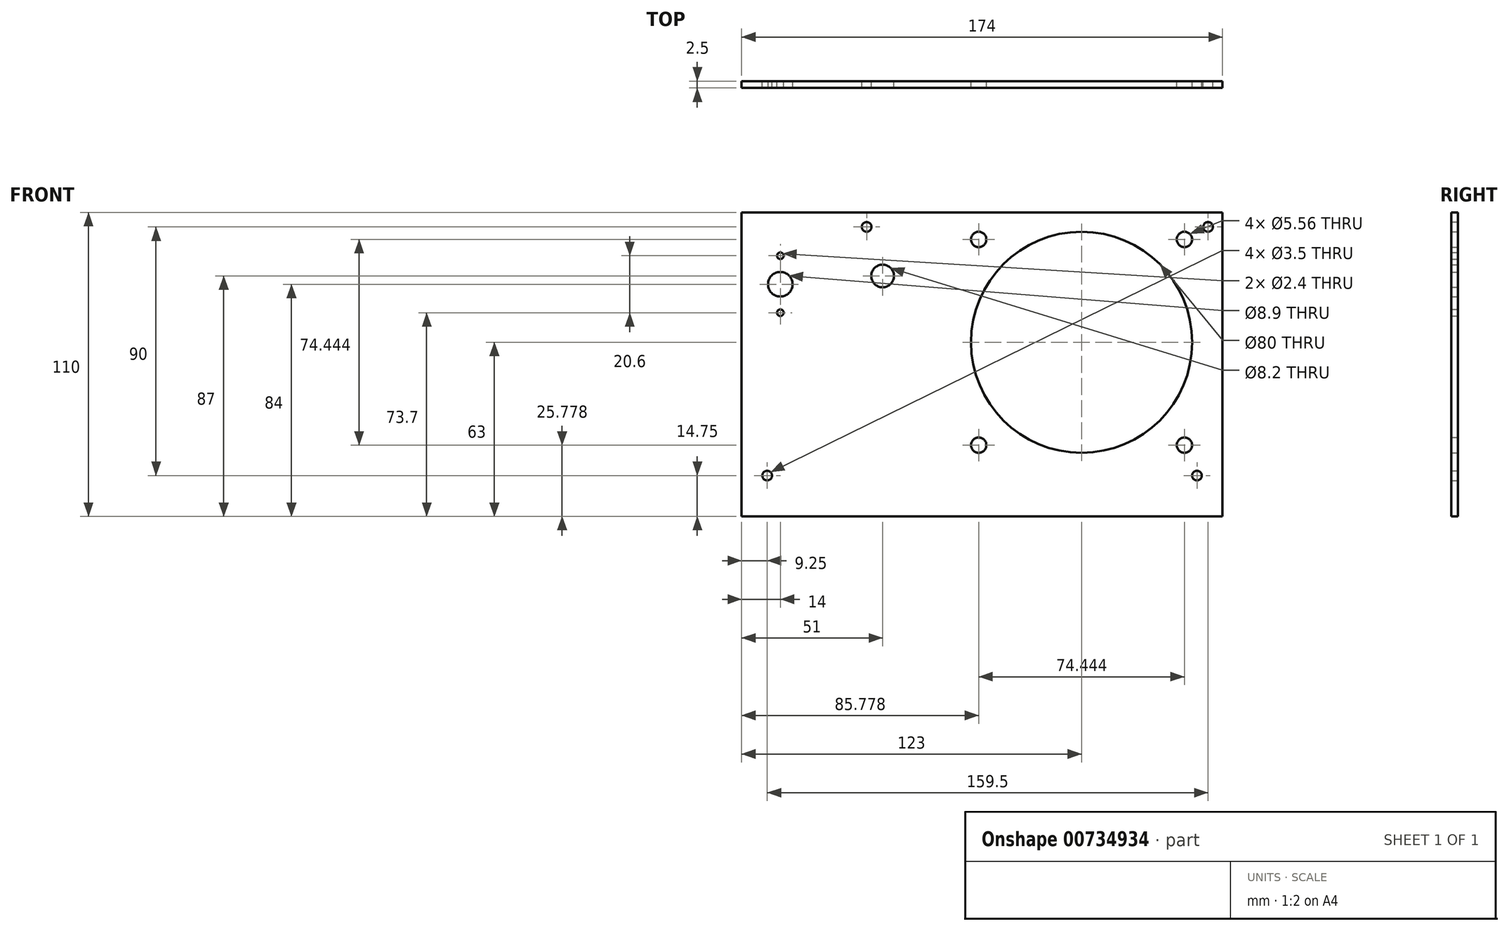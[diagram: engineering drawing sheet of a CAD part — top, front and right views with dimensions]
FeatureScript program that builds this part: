
annotation { "Feature Type Name" : "Feature", "Feature Type Description" : "" }
export const myFeature = defineFeature(function(context is Context, id is Id, definition is map)
    precondition{}
    {
        {
            var Q0;
            Q0=qCreatedBy(makeId("Front.planeOp"),FACE);
            var sketch = newSketch(context, id + "F0", { "sketchPlane" : qUnion([Q0])});
            skLineSegment(sketch, "E0.bottom", {"start": v(-87, -55) * mm, "end": v(87, -55) * mm});
            skLineSegment(sketch, "E0.top", {"start": v(-87, 55) * mm, "end": v(87, 55) * mm});
            skLineSegment(sketch, "E0.left", {"start": v(-87, -55) * mm, "end": v(-87, 55) * mm});
            skLineSegment(sketch, "E0.right", {"start": v(87, -55) * mm, "end": v(87, 55) * mm});
            skPoint(sketch, "E0.middle", {"position": v(0, 0) * mm});
            skLineSegment(sketch, "E1.bottom", {"start": v(-80, 44) * mm, "end": v(-66, 44) * mm, "construction": true});
            skLineSegment(sketch, "E1.top", {"start": v(-80, 14) * mm, "end": v(-66, 14) * mm, "construction": true});
            skLineSegment(sketch, "E1.left", {"start": v(-80, 44) * mm, "end": v(-80, 14) * mm, "construction": true});
            skLineSegment(sketch, "E1.right", {"start": v(-66, 44) * mm, "end": v(-66, 14) * mm, "construction": true});
            skLineSegment(sketch, "E2.bottom", {"start": v(-51, 43) * mm, "end": v(-21, 43) * mm, "construction": true});
            skLineSegment(sketch, "E2.top", {"start": v(-51, 21) * mm, "end": v(-21, 21) * mm, "construction": true});
            skLineSegment(sketch, "E2.left", {"start": v(-51, 43) * mm, "end": v(-51, 21) * mm, "construction": true});
            skLineSegment(sketch, "E2.right", {"start": v(-21, 43) * mm, "end": v(-21, 21) * mm, "construction": true});
            skCircle(sketch, "E3", {"center": v(-77.75, -40.25) * mm, "radius": 1.75 * mm});
            skCircle(sketch, "E4", {"center": v(81.75, 49.75) * mm, "radius": 1.75 * mm});
            skCircle(sketch, "E5", {"center": v(-41.75, 49.75) * mm, "radius": 1.75 * mm});
            skCircle(sketch, "E6", {"center": v(77.75, -40.25) * mm, "radius": 1.75 * mm});
            skLineSegment(sketch, "E7.bottom", {"start": v(76, -32) * mm, "end": v(-4, -32) * mm, "construction": true});
            skLineSegment(sketch, "E7.top", {"start": v(76, 48) * mm, "end": v(-4, 48) * mm, "construction": true});
            skLineSegment(sketch, "E7.left", {"start": v(76, -32) * mm, "end": v(76, 48) * mm, "construction": true});
            skLineSegment(sketch, "E7.right", {"start": v(-4, -32) * mm, "end": v(-4, 48) * mm, "construction": true});
            skCircle(sketch, "E8", {"center": v(36, 8) * mm, "radius": 40 * mm});
            skPoint(sketch, "E8.first.point", {"position": v(36, 48) * mm});
            skPoint(sketch, "E8.second.point", {"position": v(76, 8) * mm});
            skPoint(sketch, "E8.third.point", {"position": v(36, -32) * mm});
            skLineSegment(sketch, "E9.bottom", {"start": v(-4, 48) * mm, "end": v(1.56, 48) * mm, "construction": true});
            skLineSegment(sketch, "E9.top", {"start": v(-4, 42.44) * mm, "end": v(1.56, 42.44) * mm, "construction": true});
            skLineSegment(sketch, "E9.left", {"start": v(-4, 48) * mm, "end": v(-4, 42.44) * mm, "construction": true});
            skLineSegment(sketch, "E9.right", {"start": v(1.56, 48) * mm, "end": v(1.56, 42.44) * mm, "construction": true});
            skCircle(sketch, "E10", {"center": v(-1.22, 45.22) * mm, "radius": 2.78 * mm});
            skPoint(sketch, "E10.first.point", {"position": v(-1.22, 48) * mm});
            skPoint(sketch, "E10.second.point", {"position": v(1.56, 45.22) * mm});
            skPoint(sketch, "E10.third.point", {"position": v(-1.22, 42.44) * mm});
            skLineSegment(sketch, "E11.bottom", {"start": v(76, 48) * mm, "end": v(70.44, 48) * mm, "construction": true});
            skLineSegment(sketch, "E11.top", {"start": v(76, 42.44) * mm, "end": v(70.44, 42.44) * mm, "construction": true});
            skLineSegment(sketch, "E11.left", {"start": v(76, 48) * mm, "end": v(76, 42.44) * mm, "construction": true});
            skLineSegment(sketch, "E11.right", {"start": v(70.44, 48) * mm, "end": v(70.44, 42.44) * mm, "construction": true});
            skLineSegment(sketch, "E12.bottom", {"start": v(76, -32) * mm, "end": v(70.44, -32) * mm, "construction": true});
            skLineSegment(sketch, "E12.top", {"start": v(76, -26.44) * mm, "end": v(70.44, -26.44) * mm, "construction": true});
            skLineSegment(sketch, "E12.left", {"start": v(76, -32) * mm, "end": v(76, -26.44) * mm, "construction": true});
            skLineSegment(sketch, "E12.right", {"start": v(70.44, -32) * mm, "end": v(70.44, -26.44) * mm, "construction": true});
            skLineSegment(sketch, "E13.bottom", {"start": v(-4, -32) * mm, "end": v(1.56, -32) * mm, "construction": true});
            skLineSegment(sketch, "E13.top", {"start": v(-4, -26.44) * mm, "end": v(1.56, -26.44) * mm, "construction": true});
            skLineSegment(sketch, "E13.left", {"start": v(-4, -32) * mm, "end": v(-4, -26.44) * mm, "construction": true});
            skLineSegment(sketch, "E13.right", {"start": v(1.56, -32) * mm, "end": v(1.56, -26.44) * mm, "construction": true});
            skCircle(sketch, "E14", {"center": v(73.22, 45.22) * mm, "radius": 2.78 * mm});
            skPoint(sketch, "E14.first.point", {"position": v(73.22, 48) * mm});
            skPoint(sketch, "E14.second.point", {"position": v(70.44, 45.22) * mm});
            skPoint(sketch, "E14.third.point", {"position": v(73.22, 42.44) * mm});
            skCircle(sketch, "E15", {"center": v(73.22, -29.22) * mm, "radius": 2.78 * mm});
            skPoint(sketch, "E15.first.point", {"position": v(73.22, -26.44) * mm});
            skPoint(sketch, "E15.second.point", {"position": v(70.44, -29.22) * mm});
            skPoint(sketch, "E15.third.point", {"position": v(73.22, -32) * mm});
            skCircle(sketch, "E16", {"center": v(-1.22, -29.22) * mm, "radius": 2.78 * mm});
            skPoint(sketch, "E16.first.point", {"position": v(-1.22, -26.44) * mm});
            skPoint(sketch, "E16.second.point", {"position": v(-4, -29.22) * mm});
            skPoint(sketch, "E16.third.point", {"position": v(-1.22, -32) * mm});
            skPoint(sketch, "E17", {"position": v(-80, 29) * mm});
            skPoint(sketch, "E18", {"position": v(-73, 14) * mm});
            skPoint(sketch, "E19", {"position": v(-73, 29) * mm});
            skCircle(sketch, "E20", {"center": v(-73, 29) * mm, "radius": 4.45 * mm});
            skLineSegment(sketch, "E21", {"start": v(-73, 18.7) * mm, "end": v(-73, 39.3) * mm, "construction": true});
            skCircle(sketch, "E22", {"center": v(-73, 39.3) * mm, "radius": 1.2 * mm});
            skCircle(sketch, "E23", {"center": v(-73, 18.7) * mm, "radius": 1.2 * mm});
            skPoint(sketch, "E24", {"position": v(-51, 32) * mm});
            skPoint(sketch, "E25", {"position": v(-36, 21) * mm});
            skPoint(sketch, "E26", {"position": v(-36, 32) * mm});
            skCircle(sketch, "E27", {"center": v(-36, 32) * mm, "radius": 4.1 * mm});
            skSolve(sketch);
        }
        {
            var Q0;
            {var subQ0=sQuery(id+"F0.wireOp",EDGE,"cfSl68OW-Y9iN-8OMg-qRQz-4nlVoakqv04e");var subQ1=sQuery(id+"F0.wireOp",EDGE,"vP8uru67-1rKL-aZWj-Ed0x-q8X2hZfk60Cs.left");var subQ2=makeQuery(id+"F0.imprint","INTERSECT",VERTEX,{"derivedFrom":[subQ1,subQ0]});Q0=makeQuery(id+"F0.imprint","IMPRINT",FACE,{"disambiguationData":[TD([[makeQuery(id+"F0.imprint","IMPRINT",EDGE,{"disambiguationData":[TD([[subQ2,1.0]])],"derivedFrom":subQ1}),-1.0]])]});}
            var Q1;
            {var subQ0=sQuery(id+"F0.wireOp",EDGE,"cfSl68OW-Y9iN-8OMg-qRQz-4nlVoakqv04e");var subQ1=sQuery(id+"F0.wireOp",EDGE,"vP8uru67-1rKL-aZWj-Ed0x-q8X2hZfk60Cs.bottom");var subQ2=makeQuery(id+"F0.imprint","INTERSECT",VERTEX,{"derivedFrom":[subQ1,subQ0]});Q1=makeQuery(id+"F0.imprint","IMPRINT",FACE,{"disambiguationData":[TD([[makeQuery(id+"F0.imprint","IMPRINT",EDGE,{"disambiguationData":[TD([[subQ2,1.0]])],"derivedFrom":subQ1}),1.0]])]});}
            var Q2;
            {var subQ0=sQuery(id+"F0.wireOp",EDGE,"PTcjDCUc-MgrD-nLkz-FqYk-Pj8Vo6t2aX3y");var subQ1=sQuery(id+"F0.wireOp",EDGE,"vP8uru67-1rKL-aZWj-Ed0x-q8X2hZfk60Cs.left");var subQ2=makeQuery(id+"F0.imprint","INTERSECT",VERTEX,{"derivedFrom":[subQ1,subQ0]});Q2=makeQuery(id+"F0.imprint","IMPRINT",FACE,{"disambiguationData":[TD([[makeQuery(id+"F0.imprint","IMPRINT",EDGE,{"disambiguationData":[TD([[subQ2,-1.0]])],"derivedFrom":subQ1}),-1.0]])]});}
            var Q3;
            {var subQ0=sQuery(id+"F0.wireOp",EDGE,"PTcjDCUc-MgrD-nLkz-FqYk-Pj8Vo6t2aX3y");var subQ1=sQuery(id+"F0.wireOp",EDGE,"vP8uru67-1rKL-aZWj-Ed0x-q8X2hZfk60Cs.top");var subQ2=makeQuery(id+"F0.imprint","INTERSECT",VERTEX,{"derivedFrom":[subQ1,subQ0]});Q3=makeQuery(id+"F0.imprint","IMPRINT",FACE,{"disambiguationData":[TD([[makeQuery(id+"F0.imprint","IMPRINT",EDGE,{"disambiguationData":[TD([[subQ2,1.0]])],"derivedFrom":subQ1}),-1.0]])]});}
            var Q4;
            {var subQ0=sQuery(id+"F0.wireOp",EDGE,"e6uunRbi-GojN-M6QF-zxjB-Brp06QCMidCW");var subQ1=sQuery(id+"F0.wireOp",EDGE,"af8417be-5bd7-453a-83a2-fc172ac16551.2");var subQ2=makeQuery(id+"F0.imprint","INTERSECT",VERTEX,{"derivedFrom":[subQ1,subQ0]});Q4=makeQuery(id+"F0.imprint","IMPRINT",FACE,{"disambiguationData":[TD([[makeQuery(id+"F0.imprint","IMPRINT",EDGE,{"disambiguationData":[TD([[subQ2,-1.0]])],"derivedFrom":subQ1}),-1.0]])]});}
            var Q5;
            {var subQ0=sQuery(id+"F0.wireOp",EDGE,"Twv16H5i-imJu-2RaP-C3eQ-dalo2saDfy5s");var subQ1=sQuery(id+"F0.wireOp",EDGE,"vP8uru67-1rKL-aZWj-Ed0x-q8X2hZfk60Cs.right");var subQ2=makeQuery(id+"F0.imprint","INTERSECT",VERTEX,{"derivedFrom":[subQ1,subQ0]});Q5=makeQuery(id+"F0.imprint","IMPRINT",FACE,{"disambiguationData":[TD([[makeQuery(id+"F0.imprint","IMPRINT",EDGE,{"disambiguationData":[TD([[subQ2,1.0]])],"derivedFrom":subQ1}),1.0]])]});}
            var Q6;
            {var subQ0=sQuery(id+"F0.wireOp",EDGE,"PTcjDCUc-MgrD-nLkz-FqYk-Pj8Vo6t2aX3y");var subQ1=sQuery(id+"F0.wireOp",EDGE,"af8417be-5bd7-453a-83a2-fc172ac16551.1");var subQ2=makeQuery(id+"F0.imprint","INTERSECT",VERTEX,{"derivedFrom":[subQ1,subQ0]});Q6=makeQuery(id+"F0.imprint","IMPRINT",FACE,{"disambiguationData":[TD([[makeQuery(id+"F0.imprint","IMPRINT",EDGE,{"disambiguationData":[TD([[subQ2,-1.0]])],"derivedFrom":subQ1}),-1.0]])]});}
            var Q7;
            {var subQ0=sQuery(id+"F0.wireOp",EDGE,"e6uunRbi-GojN-M6QF-zxjB-Brp06QCMidCW");var subQ1=sQuery(id+"F0.wireOp",EDGE,"vP8uru67-1rKL-aZWj-Ed0x-q8X2hZfk60Cs.top");var subQ2=makeQuery(id+"F0.imprint","INTERSECT",VERTEX,{"derivedFrom":[subQ1,subQ0]});Q7=makeQuery(id+"F0.imprint","IMPRINT",FACE,{"disambiguationData":[TD([[makeQuery(id+"F0.imprint","IMPRINT",EDGE,{"disambiguationData":[TD([[subQ2,-1.0]])],"derivedFrom":subQ1}),-1.0]])]});}
            var Q8;
            {var subQ0=sQuery(id+"F0.wireOp",EDGE,"Twv16H5i-imJu-2RaP-C3eQ-dalo2saDfy5s");var subQ1=sQuery(id+"F0.wireOp",EDGE,"af8417be-5bd7-453a-83a2-fc172ac16551.0");var subQ2=makeQuery(id+"F0.imprint","INTERSECT",VERTEX,{"derivedFrom":[subQ1,subQ0]});Q8=makeQuery(id+"F0.imprint","IMPRINT",FACE,{"disambiguationData":[TD([[makeQuery(id+"F0.imprint","IMPRINT",EDGE,{"disambiguationData":[TD([[subQ2,-1.0]])],"derivedFrom":subQ1}),1.0]])]});}
            var Q9;
            {var subQ0=sQuery(id+"F0.wireOp",EDGE,"Twv16H5i-imJu-2RaP-C3eQ-dalo2saDfy5s");var subQ1=sQuery(id+"F0.wireOp",EDGE,"vP8uru67-1rKL-aZWj-Ed0x-q8X2hZfk60Cs.bottom");var subQ2=makeQuery(id+"F0.imprint","INTERSECT",VERTEX,{"derivedFrom":[subQ1,subQ0]});Q9=makeQuery(id+"F0.imprint","IMPRINT",FACE,{"disambiguationData":[TD([[makeQuery(id+"F0.imprint","IMPRINT",EDGE,{"disambiguationData":[TD([[subQ2,-1.0]])],"derivedFrom":subQ1}),1.0]])]});}
            var Q10;
            {var subQ0=sQuery(id+"F0.wireOp",EDGE,"e6uunRbi-GojN-M6QF-zxjB-Brp06QCMidCW");var subQ1=sQuery(id+"F0.wireOp",EDGE,"vP8uru67-1rKL-aZWj-Ed0x-q8X2hZfk60Cs.right");var subQ2=makeQuery(id+"F0.imprint","INTERSECT",VERTEX,{"derivedFrom":[subQ1,subQ0]});Q10=makeQuery(id+"F0.imprint","IMPRINT",FACE,{"disambiguationData":[TD([[makeQuery(id+"F0.imprint","IMPRINT",EDGE,{"disambiguationData":[TD([[subQ2,-1.0]])],"derivedFrom":subQ1}),1.0]])]});}
            var Q11;
            {var subQ0=sQuery(id+"F0.wireOp",EDGE,"45dMGhS0-YLeI-dV8t-4P02-Nx6Z4lcdnOo9");var subQ1=sQuery(id+"F0.wireOp",EDGE,"af8417be-5bd7-453a-83a2-fc172ac16551.0");var subQ2=makeQuery(id+"F0.imprint","INTERSECT",VERTEX,{"derivedFrom":[subQ1,subQ0]});Q11=makeQuery(id+"F0.imprint","IMPRINT",FACE,{"disambiguationData":[TD([[makeQuery(id+"F0.imprint","IMPRINT",EDGE,{"disambiguationData":[TD([[subQ2,-1.0]])],"derivedFrom":subQ1}),1.0]])]});}
            var Q12;
            Q12=makeQuery(id+"F0.imprint","IMPRINT",FACE,{"disambiguationData":[TD([[makeQuery(id+"F0.imprint","IMPRINT",EDGE,{"derivedFrom":sQuery(id+"F0.wireOp",EDGE,"E0.bottom")}),1.0]])]});
            var Q13;
            {var subQ0=sQuery(id+"F0.wireOp",EDGE,"vP8uru67-1rKL-aZWj-Ed0x-q8X2hZfk60Cs.right");var subQ1=sQuery(id+"F0.wireOp",EDGE,"vP8uru67-1rKL-aZWj-Ed0x-q8X2hZfk60Cs.top");var subQ2=makeQuery(id+"F0.imprint","INTERSECT",VERTEX,{"derivedFrom":[subQ1,subQ0]});Q13=makeQuery(id+"F0.imprint","IMPRINT",FACE,{"disambiguationData":[TD([[makeQuery(id+"F0.imprint","IMPRINT",EDGE,{"disambiguationData":[TD([[subQ2,1.0]])],"derivedFrom":subQ1}),-1.0]])]});}
            var Q14;
            {var subQ0=sQuery(id+"F0.wireOp",EDGE,"vP8uru67-1rKL-aZWj-Ed0x-q8X2hZfk60Cs.left");var subQ1=sQuery(id+"F0.wireOp",EDGE,"vP8uru67-1rKL-aZWj-Ed0x-q8X2hZfk60Cs.bottom");var subQ2=makeQuery(id+"F0.imprint","INTERSECT",VERTEX,{"derivedFrom":[subQ1,subQ0]});Q14=makeQuery(id+"F0.imprint","IMPRINT",FACE,{"disambiguationData":[TD([[makeQuery(id+"F0.imprint","IMPRINT",EDGE,{"disambiguationData":[TD([[subQ2,-1.0]])],"derivedFrom":subQ1}),1.0]])]});}
            var Q15;
            {var subQ0=sQuery(id+"F0.wireOp",EDGE,"vP8uru67-1rKL-aZWj-Ed0x-q8X2hZfk60Cs.right");var subQ1=sQuery(id+"F0.wireOp",EDGE,"vP8uru67-1rKL-aZWj-Ed0x-q8X2hZfk60Cs.bottom");var subQ2=makeQuery(id+"F0.imprint","INTERSECT",VERTEX,{"derivedFrom":[subQ1,subQ0]});Q15=makeQuery(id+"F0.imprint","IMPRINT",FACE,{"disambiguationData":[TD([[makeQuery(id+"F0.imprint","IMPRINT",EDGE,{"disambiguationData":[TD([[subQ2,1.0]])],"derivedFrom":subQ1}),1.0]])]});}
            var Q16;
            {var subQ0=sQuery(id+"F0.wireOp",EDGE,"vP8uru67-1rKL-aZWj-Ed0x-q8X2hZfk60Cs.left");var subQ1=sQuery(id+"F0.wireOp",EDGE,"vP8uru67-1rKL-aZWj-Ed0x-q8X2hZfk60Cs.top");var subQ2=makeQuery(id+"F0.imprint","INTERSECT",VERTEX,{"derivedFrom":[subQ1,subQ0]});Q16=makeQuery(id+"F0.imprint","IMPRINT",FACE,{"disambiguationData":[TD([[makeQuery(id+"F0.imprint","IMPRINT",EDGE,{"disambiguationData":[TD([[subQ2,-1.0]])],"derivedFrom":subQ1}),-1.0]])]});}
            var Q17;
            Q17=makeQuery(id+"F0.imprint","IMPRINT",FACE,{"disambiguationData":[TD([[makeQuery(id+"F0.imprint","IMPRINT",EDGE,{"derivedFrom":sQuery(id+"F0.wireOp",EDGE,"E1.bottom")}),-1.0]])]});
            var Q18;
            Q18=makeQuery(id+"F0.imprint","IMPRINT",FACE,{"disambiguationData":[TD([[makeQuery(id+"F0.imprint","IMPRINT",EDGE,{"derivedFrom":sQuery(id+"F0.wireOp",EDGE,"E2.bottom")}),-1.0]])]});
            extrude(context, id + "F1", {"entities" : qUnion([Q0, Q1, Q2, Q3, Q4, Q5, Q6, Q7, Q8, Q9, Q10, Q11, Q12, Q13, Q14, Q15, Q16, Q17, Q18]), "depth" : 2.5 * mm, "offsetDistance" : 25 * mm});
        }
    });
